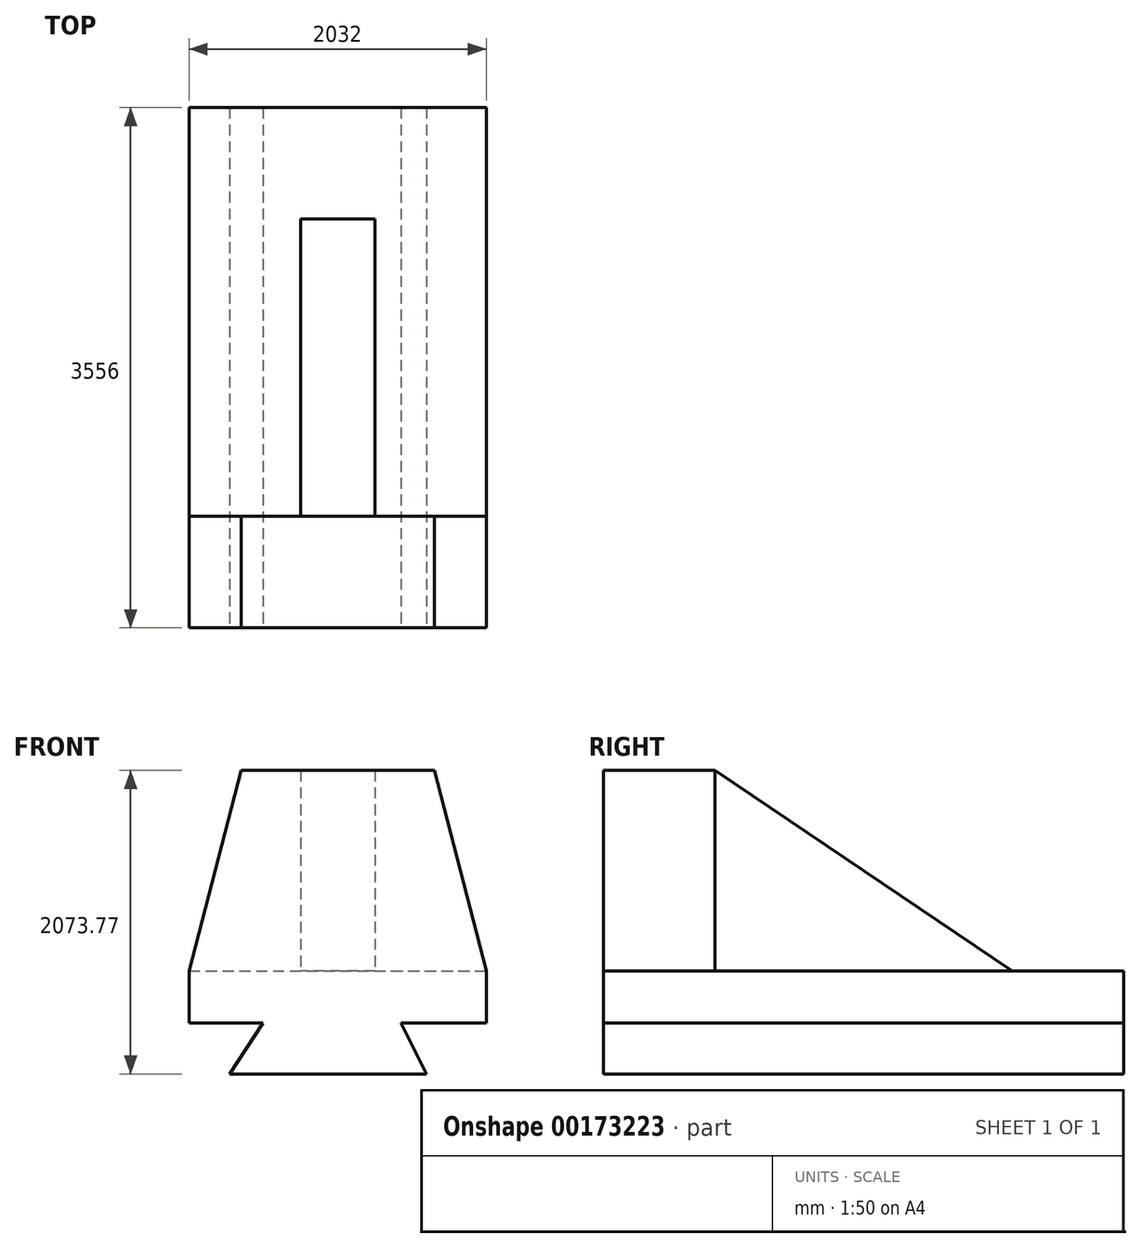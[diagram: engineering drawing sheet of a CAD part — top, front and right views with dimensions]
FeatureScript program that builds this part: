
annotation { "Feature Type Name" : "Feature", "Feature Type Description" : "" }
export const myFeature = defineFeature(function(context is Context, id is Id, definition is map)
    precondition{}
    {
        {
            var Q0;
            Q0=qCreatedBy(makeId("Top.planeOp"),FACE);
            var sketch = newSketch(context, id + "F0", { "sketchPlane" : qUnion([Q0])});
            skLineSegment(sketch, "E0.bottom", {"start": v(0, 0) * mm, "end": v(2032, 0) * mm});
            skLineSegment(sketch, "E0.top", {"start": v(0, 3556) * mm, "end": v(2032, 3556) * mm});
            skLineSegment(sketch, "E0.left", {"start": v(0, 0) * mm, "end": v(0, 3556) * mm});
            skLineSegment(sketch, "E0.right", {"start": v(2032, 0) * mm, "end": v(2032, 3556) * mm});
            skSolve(sketch);
        }
        {
            var Q0;
            Q0 = qSketchRegion(id + "F0", true);
            extrude(context, id + "F1", {"entities" : qUnion([Q0]), "oppositeDirection" : true, "depth" : 355.6 * mm});
        }
        {
            var Q0;
            Q0=makeQuery(id+"F1.opExtrude","SWEPT_FACE",FACE,{"disambiguationData":[OSD([sQuery(id+"F0.wireOp",EDGE,"E0.bottom")])]});
            var sketch = newSketch(context, id + "F2", { "sketchPlane" : qUnion([Q0])});
            skLineSegment(sketch, "E1", {"start": v(278.5, -702.17) * mm, "end": v(505.79, -355.6) * mm});
            skLineSegment(sketch, "E2", {"start": v(278.5, -702.17) * mm, "end": v(1622.34, -702.17) * mm});
            skLineSegment(sketch, "E3", {"start": v(1622.34, -702.17) * mm, "end": v(1447.72, -355.6) * mm});
            skSolve(sketch);
        }
        {
            var Q0;
            {var subQ0=sQuery(id+"F2.wireOp",EDGE,"E1");Q0=makeQuery(id+"F2.imprint","IMPRINT",FACE,{"disambiguationData":[TD([[makeQuery(id+"F2.imprint","IMPRINT",EDGE,{"derivedFrom":subQ0}),-1.0]])]});}
            extrude(context, id + "F3", {"entities" : qUnion([Q0]), "operationType" : NewBodyOperationType.ADD, "oppositeDirection" : true, "depth" : 3556 * mm});
        }
        {
            var Q0;
            {var subQ0=sQuery(id+"F0.wireOp",EDGE,"E0.bottom");Q0=makeQuery(id+"F3.boolean.opBoolean","MERGE",FACE,{"derivedFrom":[makeQuery(id+"F1.opExtrude","SWEPT_FACE",FACE,{"disambiguationData":[OSD([subQ0])]}),makeQuery(id+"F3.opExtrude","CAP_FACE",FACE,{"disambiguationData":[OSD([subQ0,sQuery(id+"F2.wireOp",EDGE,"E1"),sQuery(id+"F2.wireOp",EDGE,"E2"),sQuery(id+"F2.wireOp",EDGE,"E3")])],"isStart":true})]});}
            var sketch = newSketch(context, id + "F4", { "sketchPlane" : qUnion([Q0])});
            skLineSegment(sketch, "E4", {"start": v(0, 0) * mm, "end": v(355.6, 1371.6) * mm});
            skLineSegment(sketch, "E5", {"start": v(355.6, 1371.6) * mm, "end": v(1676.4, 1371.6) * mm});
            skLineSegment(sketch, "E6", {"start": v(1676.4, 1371.6) * mm, "end": v(2032, 0) * mm});
            skLineSegment(sketch, "E7", {"start": v(2032, 0) * mm, "end": v(0, 0) * mm});
            skSolve(sketch);
        }
        {
            var Q0;
            Q0 = qSketchRegion(id + "F4", true);
            extrude(context, id + "F5", {"entities" : qUnion([Q0]), "operationType" : NewBodyOperationType.ADD, "oppositeDirection" : true, "depth" : 762 * mm});
        }
        {
            var Q0;
            Q0=makeQuery(id+"F1.opExtrude","CAP_FACE",FACE,{"disambiguationData":[OSD([sQuery(id+"F0.wireOp",EDGE,"E0.bottom"),sQuery(id+"F0.wireOp",EDGE,"E0.top"),sQuery(id+"F0.wireOp",EDGE,"E0.left"),sQuery(id+"F0.wireOp",EDGE,"E0.right")])],"isStart":true});
            var sketch = newSketch(context, id + "F6", { "sketchPlane" : qUnion([Q0])});
            skLineSegment(sketch, "E8.bottom", {"start": v(1270, 762) * mm, "end": v(762, 762) * mm});
            skLineSegment(sketch, "E8.top", {"start": v(1270, 2794) * mm, "end": v(762, 2794) * mm});
            skLineSegment(sketch, "E8.left", {"start": v(1270, 762) * mm, "end": v(1270, 2794) * mm});
            skLineSegment(sketch, "E8.right", {"start": v(762, 762) * mm, "end": v(762, 2794) * mm});
            skSolve(sketch);
        }
        {
            var Q0;
            Q0 = qSketchRegion(id + "F6", true);
            extrude(context, id + "F7", {"entities" : qUnion([Q0]), "operationType" : NewBodyOperationType.ADD, "depth" : 1371.6 * mm});
        }
        {
            var Q0;
            Q0=makeQuery(id+"F7.opExtrude","SWEPT_FACE",FACE,{"disambiguationData":[OSD([sQuery(id+"F6.wireOp",EDGE,"E8.right")])]});
            var sketch = newSketch(context, id + "F8", { "sketchPlane" : qUnion([Q0])});
            skLineSegment(sketch, "E9", {"start": v(-762, 1371.6) * mm, "end": v(-2794, 0) * mm});
            skLineSegment(sketch, "E10", {"start": v(-2794, 0) * mm, "end": v(-2794, 1371.6) * mm});
            skLineSegment(sketch, "E11", {"start": v(-2794, 1371.6) * mm, "end": v(-762, 1371.6) * mm});
            skSolve(sketch);
        }
        {
            var Q0;
            Q0=makeQuery(id+"F8.imprint","IMPRINT",FACE,{"disambiguationData":[TD([[makeQuery(id+"F8.imprint","IMPRINT",EDGE,{"derivedFrom":sQuery(id+"F8.wireOp",EDGE,"E9")}),-1.0]])]});
            extrude(context, id + "F9", {"entities" : qUnion([Q0]), "operationType" : NewBodyOperationType.REMOVE, "endBound" : BoundingType.THROUGH_ALL, "oppositeDirection" : true, "depth" : 25.4 * mm});
        }
    });
